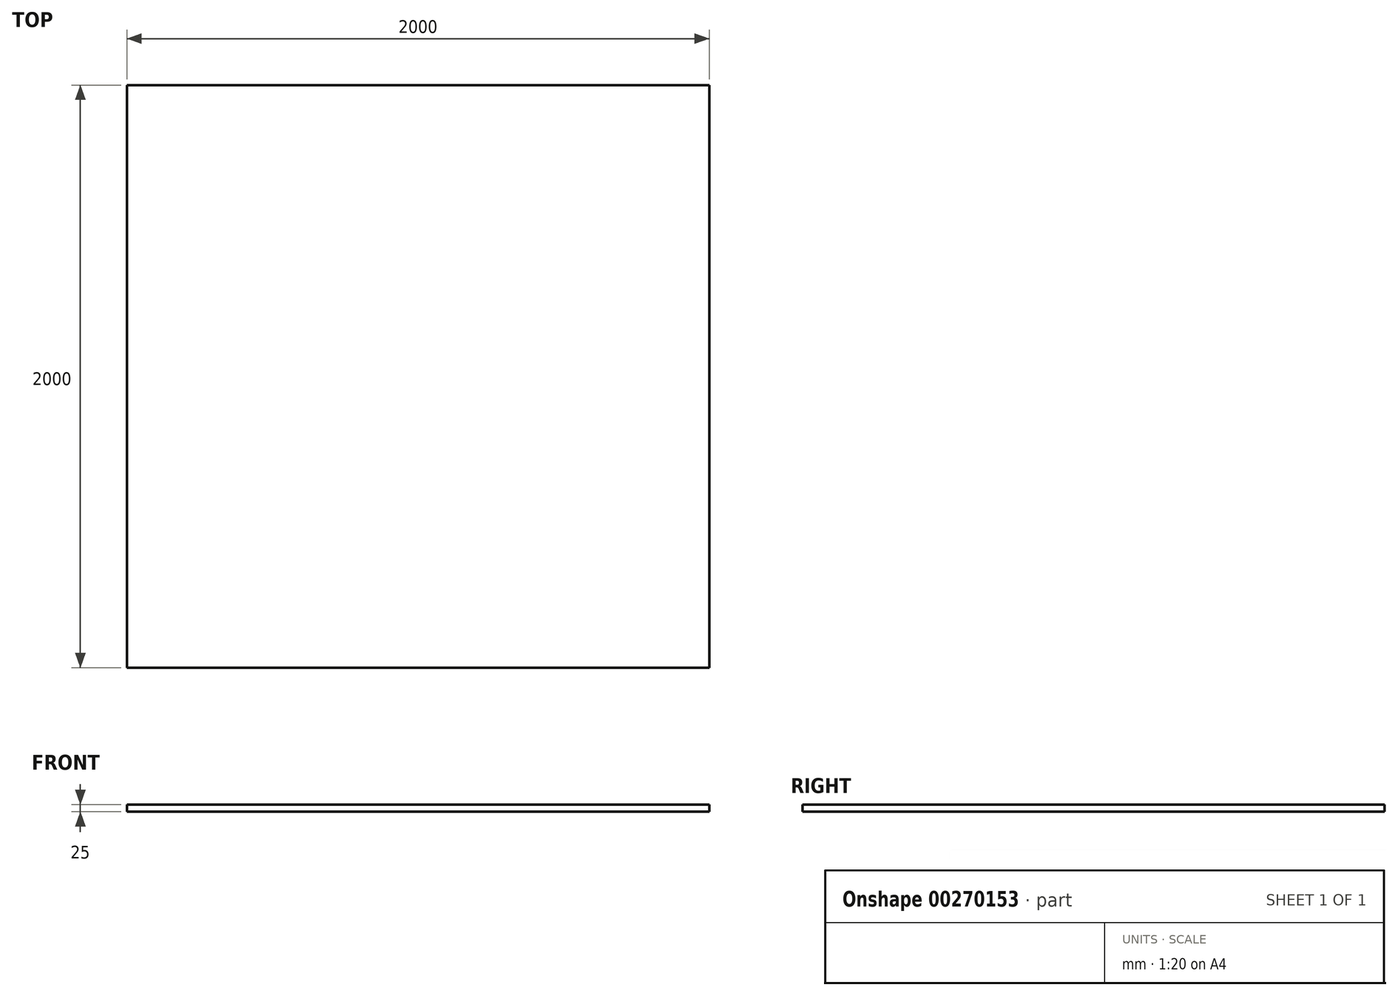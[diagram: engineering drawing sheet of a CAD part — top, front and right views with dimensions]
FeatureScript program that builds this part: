
annotation { "Feature Type Name" : "Feature", "Feature Type Description" : "" }
export const myFeature = defineFeature(function(context is Context, id is Id, definition is map)
    precondition{}
    {
        {
            var Q0;
            Q0=qCreatedBy(makeId("Top.planeOp"),FACE);
            var sketch = newSketch(context, id + "F0", { "sketchPlane" : qUnion([Q0])});
            skLineSegment(sketch, "E0.bottom", {"start": v(1000, -1000) * mm, "end": v(-1000, -1000) * mm});
            skLineSegment(sketch, "E0.top", {"start": v(1000, 1000) * mm, "end": v(-1000, 1000) * mm});
            skLineSegment(sketch, "E0.left", {"start": v(1000, -1000) * mm, "end": v(1000, 1000) * mm});
            skLineSegment(sketch, "E0.right", {"start": v(-1000, -1000) * mm, "end": v(-1000, 1000) * mm});
            skPoint(sketch, "E0.middle", {"position": v(0, 0) * mm});
            skSolve(sketch);
        }
        {
            var Q0;
            Q0 = qSketchRegion(id + "F0", true);
            extrude(context, id + "F1", {"entities" : qUnion([Q0]), "depth" : 25 * mm});
        }
    });
